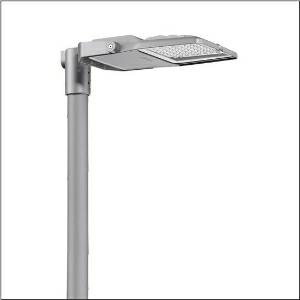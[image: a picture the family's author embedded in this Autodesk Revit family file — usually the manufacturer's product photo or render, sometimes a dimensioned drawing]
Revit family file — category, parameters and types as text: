
# Revit family: floodlight_fl_21_iq_mini___pl52_5xa7771c4d3a_e4a2
name_source: partatom
category: Lighting Fixtures
units: mm (PartAtom-declared; Revit-internal decimal feet)

## family parameters
Cut with Voids When Loaded = No
Host = Face
Light Source = No
Part Type = Normal
Room Calculation Point = No
Round Connector Dimension = Use Diameter
Shared = No

## types (1)
- --- (1 x LED, 12720 lm, 87.2 W, 4000K)
    Apparent Load = 87 VA
    CIE Flux Codes = 26 60 98 100 100
    Color Rendering = 70
    Color Temperature = 4000K
    Default Elevation = 1800 mm
    Description = Floodlight FL 21 iQ mini, floodlight, primary light control with lens, of PMMA, primary optical cover: protective disc, of toughened safety glass, transparent, light distribution: PL52, light emission: direct distribution, installation type: surface-mounted, LED, High Power LED, rated luminous flux: 12.720lm, luminous efficacy: 146lm/W, light colour: 740, colour temperature: 4000K, control gear: iQ Comfort/DALI, control: Auto-Match, Temp-Guard, Lumen-Switch, Night-Set, Smart-Wire, Light-Fading, Desk-Remote (wireless, voltage-free reading and setting of iQ features in the workshop via application-optimized NFC function/RFID function), optimised constant luminous flux control (CLO 2.0), with terminal, 6-pole, mains connection: 220..240V, AC, 50/60Hz, start of lifetime: 87W, end of service life: 92W, reduction: 40W, luminaire housing, of diecast aluminium, powder-coated, Siteco® metallic grey (DB 702S), corrosivity category C5 mid according to DIN EN ISO 12944, suitable for swimming pools, chlorine-resistant, sealing non-destructively replaceable, please order mast flange separately, mast bracket, of steel, galvanised, powder-coated, Siteco® metallic grey (DB 702S), protection rating (complete): IP66, insulation class (complete): insulation class II (safety insulation), certification: CE, ENEC, VDE, protection symbol: D, impact resistance: IK08, permissible operating ambient temperature: -40..+40°C, permissible operating ambient temperature for outdoor applications: -40..+50°C, standard: DIN EN 12944, LABS conformity tested according to VDMA 24364:2018-05, packaging unit: 1 piece

Light Distribution: PL52
    Height = 70 mm
    Lamp = 1 x LED
    Lamp Light Flux = 12720 lm
    Lamp Power = 87.2 W
    Lamp count = 1
    Length = 485 mm
    Luminous efficacy = 146 lm/W
    Manufacturer = Siteco
    ModVariant = No
    Model = 5XA7771C4D3A
    Number of Poles = 1
    OnlyDefault = Yes
    Power Factor = 1
    Product Name = Floodlight FL 21 iQ mini | PL52
    Product group = floodlight | pylon annexe
    ProductGroupID = 6201
    Protection Class = Protection class II
    Protection Degree = IP 66
    RLX_Detail_Level = 1
    RLX_Emergency_Light_Flux = 0 lm
    RLX_Emergency_Type = 0
    RLX_Emergency_Type_DB = No
    RlxData = <blob elided: 101437 chars, md5=368bc6d9>
    Socket = socket
    Standby Power = 0 W
    System Light Flux = 12720 lm
    System Power = 87 W
    Type Comments = factory setting: luminous flux: 100 % | dim-lin: 254 | 456 mA
    Type Image = l_1007125.jpg
    URL = http://relux.com
    VarID = @adj_185905
    Voltage = 0 V
    Weight = 0.00 kg
    Width = 337 mm

## geometry (parser evidence)
native form markers: Blend x4, Sweep x12
no freeform markers — native parametric forms only
